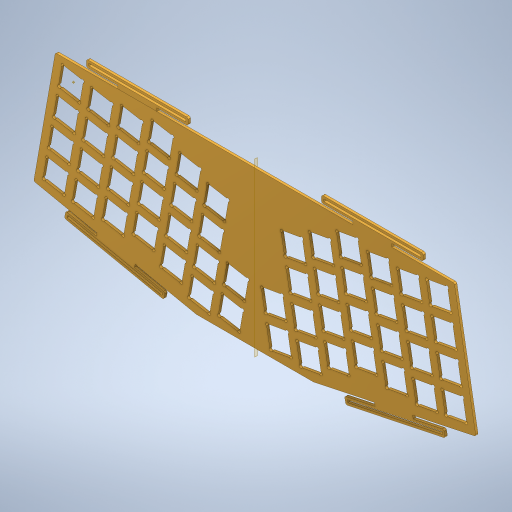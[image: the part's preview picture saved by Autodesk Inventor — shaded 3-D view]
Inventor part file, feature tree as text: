
AUTODESK INVENTOR PART (.ipt)
format: ipt  version: 2023 (Build 270158000, 158)  size: 1,413,120 bytes
history: native  units: mm
features: reference x11, other x6, sketch x5, extrude x3, plane x1, mirror x1, fillet x1, projected_geometry x1
ambient origin geometry x8: Origin, YZ Plane, XZ Plane, XY Plane, X Axis, Y Axis, Z Axis, Center Point
bodies: Body1 (feature_tree)
feature tree (29):
  extrude  "Extrusion2"  Depth=2.0mm
  extrude  "Extrusion3"  Depth=2.0mm
  sketch  "Sketch3"  dims[d12=0.47mm]
  other  "Work Point1"
  sketch  "Sketch Driven Pattern1"  dims[d1=2.0mm d2=2.0mm]
  plane  "Work Plane1"
  mirror  "Mirror1"
  extrude  "Extrusion4"  Depth=1.5mm TaperAngle=0.0deg
  fillet  "Fillet2"  Radius=13.0mm
  sketch  "Sketch1"  dims[d3=2.0mm d4=2.0mm]
  reference  "Reference1"
  reference  "Reference2"
  reference  "Reference3"
  reference  "Reference4"
  reference  "Reference5"
  reference  "Reference6"
  reference  "Reference7"
  sketch  "Sketch2"  dims[d5=2.0mm d9=1.5mm d10=0.0mm d11=13.0mm]
  reference  "Reference8"
  reference  "Reference9"
  reference  "Reference10"
  reference  "Reference11"
  sketch  "Sketch4"  dims[d13=2.0mm d14=2.0mm d15=2.0mm d16=2.0mm d17=1.5mm d18=0.0mm d19=1.5mm d20=1.5mm d21=2.0mm d22=20.0mm d23=20.0mm d24=25.0mm d25=40.0mm d26=1.5mm d27=1.5mm d28=2.0mm d29=20.0mm d30=20.0mm d31=25.0mm d32=40.0mm d33=1.5mm d34=0.0mm d36=1.0mm d35=0.5mm d37=0.0mm d38=0.0mm d39=0.0mm]
  projected_geometry  "Projected Loop1"
  other  "<userpath>\Documents\Inventor\atreus-52\Assembly.iam"
  other  "Assembly.iam"
  other  "atreus52_hotswap:1"
  other  "asm_mx_asm_PLATE:1"
  other  "asm_mx_asm_PLATE:2"
